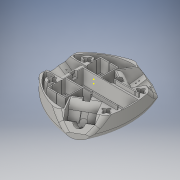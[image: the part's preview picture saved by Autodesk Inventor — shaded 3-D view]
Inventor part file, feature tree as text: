
AUTODESK INVENTOR PART (.ipt)
format: ipt  version: 2016 (Build 200138000, 138)  size: 1,409,024 bytes
history: native  units: in
note: dims shown in document units (in); Inventor stores cm internally (conversion verified against a paired STEP export)
features: sketch x82, extrude x40, fillet x14, hole x7, chamfer x3, other x1, projected_geometry x1, revolve x1
ambient origin geometry x8: Origin, YZ Plane, XZ Plane, XY Plane, X Axis, Y Axis, Z Axis, Center Point
bodies: Solid1 (feature_tree)
feature tree (149):
  extrude  "Extrusion1"  Depth=1.9685in TaperAngle=0.0deg
  extrude  "Extrusion2"  Depth=2.874in TaperAngle=0.0deg
  extrude  "Extrusion3"  Depth=1.378in
  extrude  "Extrusion4"  Depth=0.0787in
  chamfer  "Chamfer1"  Distance=1.378in
  chamfer  "Chamfer2"  Distance=1.378in
  chamfer  "Chamfer3"  Distance=1.378in
  sketch  "Sketch5"  dims[d50=270.0deg]
  sketch  "Sketch12"  dims[d51=0.9843in d52=1.378in d53=0.0in]
  sketch  "Sketch13"  dims[d54=0.9843in d55=1.378in d56=0.0in]
  extrude  "Extrusion11"  Depth=1.378in TaperAngle=0.0deg
  extrude  "Extrusion12"  Depth=0.5906in
  extrude  "Extrusion13"  Depth=0.5906in
  extrude  "Extrusion17"  Depth=0.5906in
  sketch  "Sketch32"  dims[d82=0.2756in d83=0.1969in d84=0.0in]
  sketch  "Sketch33"  dims[d85=0.7874in d86=0.1969in d87=0.0in d88=0.9843in d89=0.5906in d90=0.2756in]
  extrude  "Extrusion18"  Depth=0.1969in TaperAngle=0.0deg
  extrude  "Extrusion19"  Depth=0.1969in TaperAngle=0.0deg
  fillet  "Fillet2"  Radius=0.9843in
  fillet  "Fillet3"  Radius=0.5906in
  fillet  "Fillet4"  Radius=0.2756in
  extrude  "Extrusion20"  Depth=0.7874in
  extrude  "Extrusion21"  Depth=0.9843in
  sketch  "Sketch44"  dims[d102=0.1969in d103=0.0in d104=0.6693in]
  extrude  "Extrusion22"  Depth=0.5906in
  extrude  "Extrusion23"  Depth=0.7874in
  extrude  "Extrusion24"  Depth=0.1969in
  extrude  "Extrusion25"  Depth=0.3937in
  extrude  "Extrusion26"  Depth=0.1969in
  extrude  "Extrusion27"  Depth=0.3937in
  extrude  "Extrusion28"  Depth=0.1969in
  extrude  "Extrusion29"  Depth=0.3937in
  extrude  "Extrusion30"  Depth=1.9685in TaperAngle=0.0deg
  extrude  "Extrusion31"  Depth=1.9685in TaperAngle=0.0deg
  extrude  "Extrusion33"  Depth=1.7717in
  extrude  "Extrusion34"  Depth=0.5906in
  extrude  "Extrusion35"  Depth=0.5906in
  extrude  "Extrusion36"  Depth=0.5906in
  fillet  "Fillet5"  Radius=0.5906in
  fillet  "Fillet6"  Radius=0.5906in
  fillet  "Fillet7"  Radius=0.5906in
  fillet  "Fillet8"  Radius=0.5906in
  fillet  "Fillet9"  Radius=0.6299in
  fillet  "Fillet10"  Radius=0.6299in
  fillet  "Fillet11"  Radius=0.9055in
  fillet  "Fillet12"  Radius=0.6299in
  fillet  "Fillet13"  Radius=0.1181in
  sketch  "Sketch70"  dims[d168=0.315in d169=0.1181in]
  sketch  "Sketch71"  dims[d170=0.1181in d171=0.4724in]
  sketch  "Sketch72"  dims[d172=0.315in d173=0.4724in]
  sketch  "Sketch73"  dims[d174=0.315in d175=0.1181in]
  sketch  "Sketch74"  dims[d176=0.1181in d177=0.4724in]
  extrude  "Extrusion37"  Depth=0.4724in
  sketch  "Sketch75"  dims[d178=0.315in d179=0.4724in]
  extrude  "Extrusion38"  Depth=0.4724in
  sketch  "Sketch77"  dims[d181=0.1181in d182=0.2362in d183=0.1575in d184=0.0787in d185=90.0deg d186=0.5512in d187=0.8108in]
  extrude  "Extrusion39"  Depth=0.1181in
  sketch  "Sketch80"  dims[d195=0.1181in d196=0.2362in d197=0.1575in d198=0.0787in d199=90.0deg d200=0.5512in d201=0.8108in d230=0.9843in]
  sketch  "Sketch81"  dims[d231=2.874in d233=60.0deg]
  sketch  "Sketch82"  dims[d234=60.0deg d235=7.2936in]
  sketch  "Sketch88"  dims[d236=7.2936in d237=7.2935in]
  sketch  "Sketch89"  dims[d238=60.0deg d239=60.0deg]
  sketch  "Sketch90"  dims[d241=1.437in d242=4.7621in]
  sketch  "Sketch91"  dims[d243=0.9843in d245=0.5583in]
  sketch  "Sketch92"  dims[d248=0.2362in d249=0.0in d251=0.0787in]
  sketch  "Sketch93"  dims[d252=0.2362in d253=0.0in d255=0.0787in]
  hole  "Hole2"  [1 undecoded]
  hole  "Hole3"  [1 undecoded]
  hole  "Hole4"  [1 undecoded]
  extrude  "Extrusion42"  Depth=0.4724in
  sketch  "Sketch113"  dims[d259=1.7323in d260=0.0787in d261=1.7323in d262=1.7323in]
  extrude  "Extrusion43"  Depth=0.4724in
  extrude  "Extrusion44"  Depth=0.9843in
  sketch  "Sketch117"  dims[d288=0.0787in d293=0.0787in]
  sketch  "Sketch118"  dims[d298=0.0787in]
  extrude  "Extrusion45"  TaperAngle=60.0deg  [1 undecoded]
  hole  "Hole5"  [1 undecoded]
  extrude  "Extrusion46"  Depth=7.2935in
  sketch  "Sketch121"  dims[d314=0.3937in]
  sketch  "Sketch122"  dims[d315=0.3937in]
  sketch  "Sketch123"  dims[d320=0.0709in]
  sketch  "Sketch124"  dims[d323=0.0906in]
  sketch  "Sketch127"  dims[d324=0.3937in d325=0.0in]
  sketch  "Sketch128"  dims[d330=0.1378in]
  sketch  "Sketch129"  dims[d331=0.1378in]
  sketch  "Sketch130"  dims[d332=0.1378in]
  sketch  "Sketch131"  dims[d334=0.1378in]
  sketch  "Sketch132"  dims[d335=0.1378in]
  extrude  "Extrusion48"  TaperAngle=60.0deg  [1 undecoded]
  hole  "Hole6"  [1 undecoded]
  sketch  "Sketch133"  dims[d336=0.1378in]
  sketch  "Sketch134"  dims[d337=0.1378in]
  sketch  "Sketch135"  dims[d338=0.1378in]
  sketch  "Sketch136"  dims[d339=0.1378in]
  sketch  "Sketch137"  dims[d340=0.1378in]
  extrude  "Extrusion49"  Depth=0.9843in
  hole  "Hole7"  [1 undecoded]
  hole  "Hole8"  [1 undecoded]
  sketch  "Sketch138"  dims[d341=0.1378in]
  extrude  "Extrusion50"  Depth=1.7323in
  extrude  "Extrusion51"  Depth=0.0787in
  fillet  "Fillet19"  Radius=1.7323in
  fillet  "Fillet20"  Radius=1.7323in
  sketch  "Sketch142"  dims[d343=0.1378in]
  extrude  "Extrusion52"  Depth=1.378in TaperAngle=0.0deg
  extrude  "Extrusion53"  Depth=0.0787in
  sketch  "Sketch145"  dims[d346=0.1378in]
  sketch  "Sketch146"  dims[d347=1.4567in]
  sketch  "Sketch147"  dims[d348=1.4567in]
  sketch  "Sketch148"  dims[d349=1.4567in d350=1.4567in d351=1.4567in d352=1.4567in d356=0.0709in d357=2.1457in d358=0.0906in d359=2.1457in d360=2.1938in d361=0.1144in d362=0.1122in d366=0.1772in d367=0.4724in d375=0.4724in d376=0.1772in d377=0.1181in d378=0.1181in d379=0.1181in d380=0.1181in d381=0.2756in d382=0.2756in d383=0.2756in d384=0.2756in d385=0.4724in d386=0.1772in d387=0.1772in d388=0.4724in d389=0.7874in d390=0.0in d391=0.1181in d392=0.2362in d393=0.1575in d394=0.0787in d395=90.0deg d396=1.378in d397=0.8108in d398=0.4724in d399=0.1772in d400=0.1772in d401=0.4724in d402=0.1181in d403=0.1181in d404=0.1181in d405=0.1181in d406=0.2756in d407=0.2756in d408=0.2756in d409=0.2756in d410=0.7874in d411=0.0in d412=0.1181in d413=0.2362in d414=0.1575in d415=0.0787in d416=90.0deg d417=1.378in d418=0.8108in d419=0.1181in d420=0.2362in d421=0.1575in d422=0.0787in d423=90.0deg d424=1.378in d425=0.8108in d426=0.1181in d428=0.1181in d429=1.5748in d430=0.0in d431=0.4921in d432=0.4921in d433=0.0394in d434=1.378in d435=0.0in d436=3.1496in d437=3.1496in d438=0.7874in d439=0.0394in d440=0.9843in d441=0.0in d442=0.7874in d443=0.0394in d444=0.9843in d445=0.0in]
  sketch  "Sketch1"  dims[d13=1.9685in d14=0.0in d15=2.874in d16=0.0in]
  sketch  "Sketch2"  dims[d17=2.874in d18=0.0in d19=2.874in d20=0.0in]
  sketch  "Sketch3"  dims[d21=1.378in d22=0.0787in d23=0.2405in d24=1.378in d25=0.0787in d26=0.2405in]
  sketch  "Sketch4"  dims[d27=1.378in d28=0.0787in d29=0.2405in d49=19.685in]
  sketch  "Sketch14"  dims[d57=0.9843in d58=1.378in d59=0.0in]
  other  "Srf1"
  sketch  "Sketch16"  dims[d68=1.378in d69=0.0in d70=1.378in d71=0.0in]
  sketch  "Sketch17"  dims[d72=1.378in d73=0.0in d75=0.5906in]
  sketch  "Sketch18"  dims[d76=0.5906in d77=0.5906in]
  sketch  "Sketch31"  dims[d78=0.9843in d81=0.5906in]
  sketch  "Sketch34"  dims[d91=0.1969in d92=0.0in d93=0.7874in]
  sketch  "Sketch36"  dims[d94=0.1969in d95=0.0in d96=0.9843in]
  sketch  "Sketch42"  dims[d97=0.5906in d98=0.2756in]
  sketch  "Sketch43"  dims[d99=0.1969in d100=0.0in d101=0.7874in]
  sketch  "Sketch47"  dims[d105=0.2362in d106=0.0in d107=0.3937in]
  sketch  "Sketch49"  dims[d108=0.1969in d109=0.0in d110=0.6693in]
  sketch  "Sketch50"  dims[d111=0.2362in d112=0.0in d113=0.3937in]
  sketch  "Sketch52"  dims[d114=0.1969in d115=0.0in d116=0.6693in]
  sketch  "Sketch53"  dims[d117=0.2362in d118=0.0in d119=0.3937in]
  sketch  "Sketch55"  dims[d120=0.1969in d121=0.0in d126=1.9685in d127=0.0in]
  sketch  "Sketch56"  dims[d128=1.9685in d129=0.0in d130=1.9685in d131=0.0in]
  sketch  "Sketch57"  dims[d132=5.9055in d133=1.7717in]
  sketch  "Sketch58"  dims[d134=1.5748in d135=0.0in d136=0.5906in]
  sketch  "Sketch62"  dims[d137=0.5906in d138=0.5906in]
  sketch  "Sketch67"  dims[d139=0.5906in d140=0.5906in d141=0.5906in d142=0.5906in d143=0.5906in d144=0.5906in d145=0.6299in d146=0.0in d147=0.6299in d148=0.0in d149=0.9055in d150=0.6299in d151=0.0in d163=0.1181in]
  sketch  "Sketch68"  dims[d164=0.1181in d165=0.4724in]
  sketch  "Sketch69"  dims[d166=0.315in d167=0.4724in]
  sketch  "Sketch76"  dims[d180=0.315in]
  sketch  "Sketch78"  dims[d188=0.1181in d189=0.2362in d190=0.1575in d191=0.0787in d192=90.0deg d193=0.5512in d194=0.8108in]
  sketch  "Sketch112"  dims[d256=0.2362in d257=0.0in d258=1.7323in]
  sketch  "Sketch114"  dims[d263=0.0787in d264=1.378in d265=0.0in]
  sketch  "Sketch115"  dims[d270=0.0787in d283=0.0787in]
  sketch  "Sketch119"  dims[d303=0.0787in]
  sketch  "Sketch120"  dims[d304=0.0787in d305=0.2362in d306=0.1575in d307=0.0787in d308=90.0deg d309=0.315in d310=0.8108in]
  projected_geometry  "Projected Loop1"
  sketch  "Sketch141"  dims[d342=0.1378in]
  sketch  "Sketch143"  dims[d344=0.1378in]
  sketch  "Sketch144"  dims[d345=0.1378in]
  revolve  "RevolutionSrf1"  [1 undecoded]
note: 10 required parameter values undecoded (feature->parameter linkage not recoverable at this tier; creation-order binding heuristic only, values carry confidence <= 0.55)